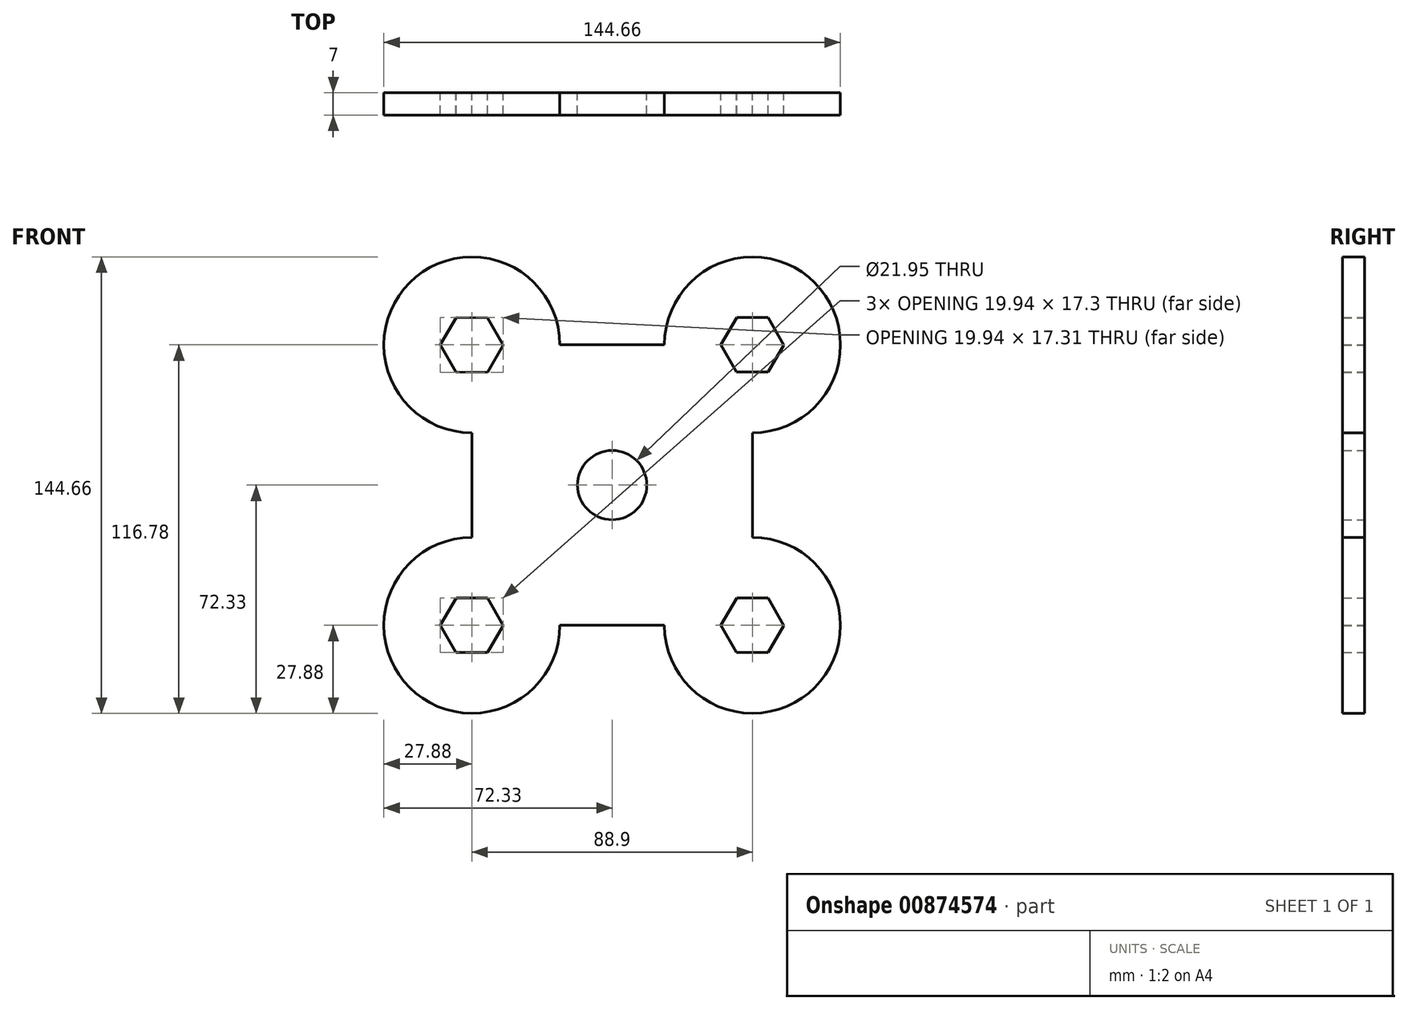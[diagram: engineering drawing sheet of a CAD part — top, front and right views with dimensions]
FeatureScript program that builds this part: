
annotation { "Feature Type Name" : "Feature", "Feature Type Description" : "" }
export const myFeature = defineFeature(function(context is Context, id is Id, definition is map)
    precondition{}
    {
        {
            var Q0;
            Q0=qCreatedBy(makeId("Front.planeOp"),FACE);
            var sketch = newSketch(context, id + "F0", { "sketchPlane" : qUnion([Q0])});
            skLineSegment(sketch, "E0.bottom", {"start": v(44.45, 44.45) * mm, "end": v(-44.45, 44.45) * mm});
            skLineSegment(sketch, "E0.top", {"start": v(44.45, -44.45) * mm, "end": v(-44.45, -44.45) * mm});
            skLineSegment(sketch, "E0.left", {"start": v(44.45, 44.45) * mm, "end": v(44.45, -44.45) * mm});
            skLineSegment(sketch, "E0.right", {"start": v(-44.45, 44.45) * mm, "end": v(-44.45, -44.45) * mm});
            skPoint(sketch, "E0.middle", {"position": v(0, 0) * mm});
            skCircle(sketch, "E1", {"center": v(0, 0) * mm, "radius": 10.97 * mm});
            skCircle(sketch, "E2", {"center": v(-44.45, 44.45) * mm, "radius": 27.88 * mm});
            skCircle(sketch, "E3", {"center": v(44.45, 44.45) * mm, "radius": 27.88 * mm});
            skCircle(sketch, "E4", {"center": v(-44.45, -44.45) * mm, "radius": 27.88 * mm});
            skCircle(sketch, "E5", {"center": v(44.45, -44.45) * mm, "radius": 27.88 * mm});
            skCircle(sketch, "E6.cCircle", {"center": v(44.45, -44.45) * mm, "radius": 8.64 * mm, "construction": true});
            skLineSegment(sketch, "E6.0", {"start": v(34.48, -44.42) * mm, "end": v(39.49, -35.8) * mm});
            skLineSegment(sketch, "E6.1", {"start": v(39.49, -35.8) * mm, "end": v(49.46, -35.83) * mm});
            skLineSegment(sketch, "E6.2", {"start": v(49.46, -35.83) * mm, "end": v(54.42, -44.48) * mm});
            skLineSegment(sketch, "E6.3", {"start": v(54.42, -44.48) * mm, "end": v(49.41, -53.1) * mm});
            skLineSegment(sketch, "E6.4", {"start": v(49.41, -53.1) * mm, "end": v(39.44, -53.07) * mm});
            skLineSegment(sketch, "E6.5", {"start": v(39.44, -53.07) * mm, "end": v(34.48, -44.42) * mm});
            skPoint(sketch, "E6.0.midPoint", {"position": v(36.98, -40.11) * mm});
            skCircle(sketch, "E7.cCircle", {"center": v(-44.45, -44.45) * mm, "radius": 8.64 * mm, "construction": true});
            skLineSegment(sketch, "E7.0", {"start": v(-54.42, -44.42) * mm, "end": v(-49.41, -35.8) * mm});
            skLineSegment(sketch, "E7.1", {"start": v(-49.41, -35.8) * mm, "end": v(-39.44, -35.83) * mm});
            skLineSegment(sketch, "E7.2", {"start": v(-39.44, -35.83) * mm, "end": v(-34.48, -44.48) * mm});
            skLineSegment(sketch, "E7.3", {"start": v(-34.48, -44.48) * mm, "end": v(-39.49, -53.1) * mm});
            skLineSegment(sketch, "E7.4", {"start": v(-39.49, -53.1) * mm, "end": v(-49.46, -53.07) * mm});
            skLineSegment(sketch, "E7.5", {"start": v(-49.46, -53.07) * mm, "end": v(-54.42, -44.42) * mm});
            skPoint(sketch, "E7.0.midPoint", {"position": v(-51.92, -40.11) * mm});
            skCircle(sketch, "E8.cCircle", {"center": v(44.45, 44.45) * mm, "radius": 8.64 * mm, "construction": true});
            skLineSegment(sketch, "E8.0", {"start": v(34.48, 44.48) * mm, "end": v(39.49, 53.1) * mm});
            skLineSegment(sketch, "E8.1", {"start": v(39.49, 53.1) * mm, "end": v(49.46, 53.07) * mm});
            skLineSegment(sketch, "E8.2", {"start": v(49.46, 53.07) * mm, "end": v(54.42, 44.42) * mm});
            skLineSegment(sketch, "E8.3", {"start": v(54.42, 44.42) * mm, "end": v(49.41, 35.8) * mm});
            skLineSegment(sketch, "E8.4", {"start": v(49.41, 35.8) * mm, "end": v(39.44, 35.83) * mm});
            skLineSegment(sketch, "E8.5", {"start": v(39.44, 35.83) * mm, "end": v(34.48, 44.48) * mm});
            skPoint(sketch, "E8.0.midPoint", {"position": v(36.98, 48.79) * mm});
            skCircle(sketch, "E9.cCircle", {"center": v(-44.45, 44.45) * mm, "radius": 8.64 * mm, "construction": true});
            skLineSegment(sketch, "E9.0", {"start": v(-54.42, 44.49) * mm, "end": v(-49.4, 53.1) * mm});
            skLineSegment(sketch, "E9.1", {"start": v(-49.4, 53.1) * mm, "end": v(-39.43, 53.07) * mm});
            skLineSegment(sketch, "E9.2", {"start": v(-39.43, 53.07) * mm, "end": v(-34.48, 44.41) * mm});
            skLineSegment(sketch, "E9.3", {"start": v(-34.48, 44.41) * mm, "end": v(-39.5, 35.8) * mm});
            skLineSegment(sketch, "E9.4", {"start": v(-39.5, 35.8) * mm, "end": v(-49.47, 35.83) * mm});
            skLineSegment(sketch, "E9.5", {"start": v(-49.47, 35.83) * mm, "end": v(-54.42, 44.49) * mm});
            skPoint(sketch, "E9.0.midPoint", {"position": v(-51.91, 48.8) * mm});
            skSolve(sketch);
        }
        {
            var Q0;
            Q0 = qSketchRegion(id + "F0", true);
            extrude(context, id + "F1", {"entities" : qUnion([Q0]), "depth" : 7 * mm, "offsetDistance" : 25.4 * mm});
        }
    });
